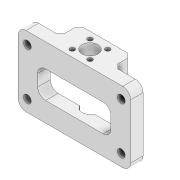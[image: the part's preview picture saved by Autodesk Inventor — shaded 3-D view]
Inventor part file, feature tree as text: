
AUTODESK INVENTOR PART (.ipt)
format: ipt  version: 2020 (Build 240168000, 168)  size: 131,072 bytes
history: native  units: mm
features: chamfer x1
ambient origin geometry x8: Origin, YZ Plane, XZ Plane, XY Plane, X Axis, Y Axis, Z Axis, Center Point
bodies: Solid1 (feature_tree)
feature tree (1):
  chamfer  "Chamfer3"  [1 undecoded]
note: 1 required parameter value undecoded (feature->parameter linkage not recoverable at this tier; creation-order binding heuristic only, values carry confidence <= 0.55)
